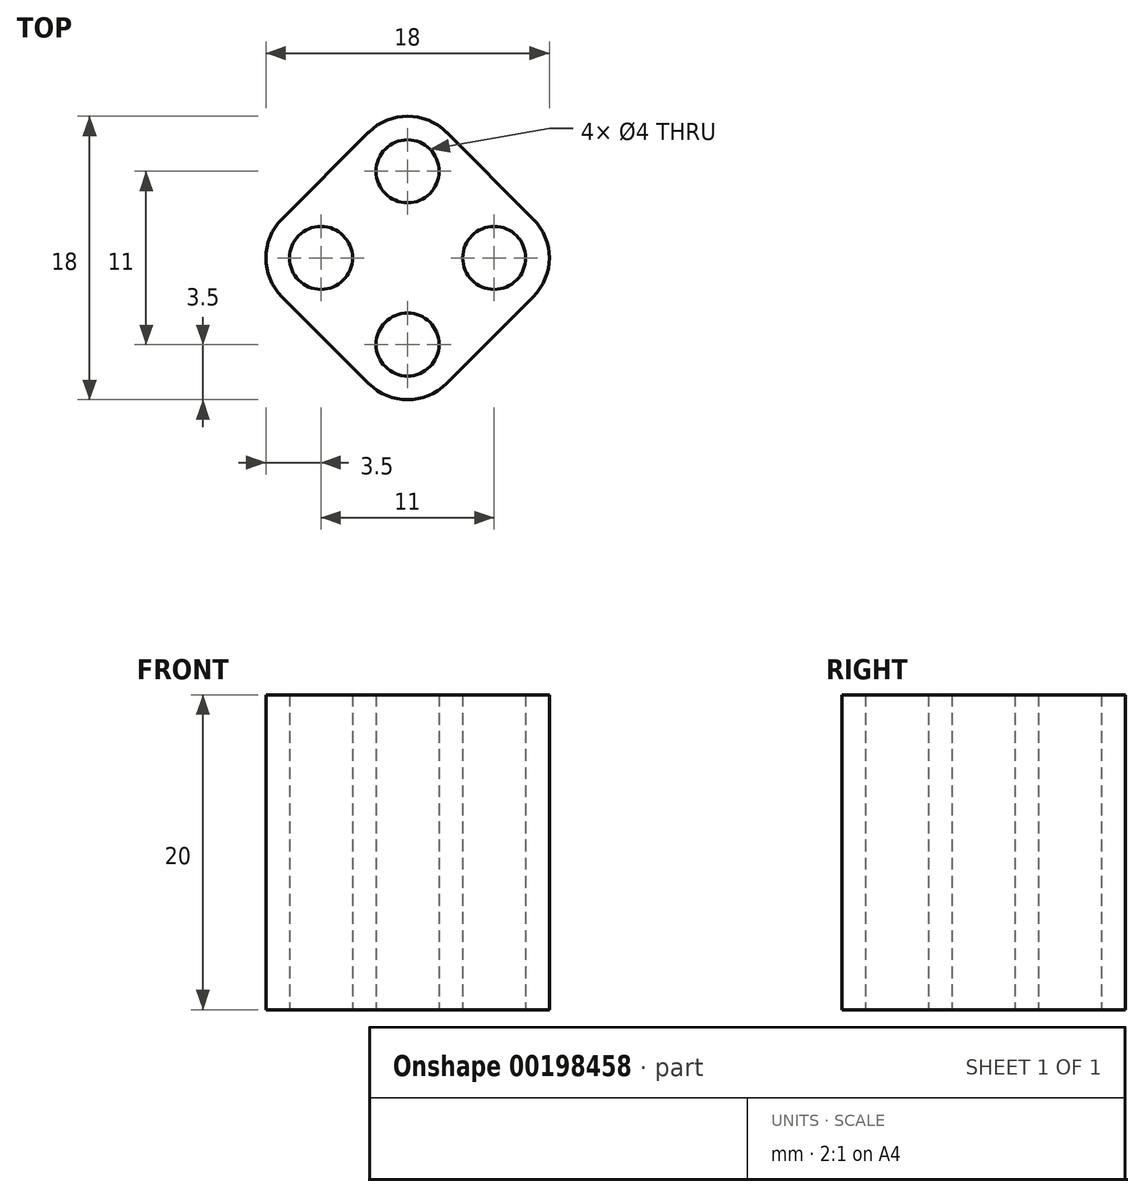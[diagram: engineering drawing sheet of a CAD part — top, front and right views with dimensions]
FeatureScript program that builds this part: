
annotation { "Feature Type Name" : "Feature", "Feature Type Description" : "" }
export const myFeature = defineFeature(function(context is Context, id is Id, definition is map)
    precondition{}
    {
        {
            var Q0;
            Q0=qCreatedBy(makeId("Top.planeOp"),FACE);
            var sketch = newSketch(context, id + "F0", { "sketchPlane" : qUnion([Q0])});
            skArc(sketch, "E0", {"start": v(-7.97, 2.47) * mm, "mid": v(-9, 0) * mm, "end": v(-7.97, -2.47) * mm});
            skCircle(sketch, "E1", {"center": v(-5.5, 0) * mm, "radius": 2 * mm});
            skArc(sketch, "E2.1.0", {"start": v(-2.47, -7.97) * mm, "mid": v(0, -9) * mm, "end": v(2.47, -7.97) * mm});
            skCircle(sketch, "E2.1.1", {"center": v(0, -5.5) * mm, "radius": 2 * mm});
            skArc(sketch, "E2.2.0", {"start": v(7.97, -2.47) * mm, "mid": v(9, 0) * mm, "end": v(7.97, 2.47) * mm});
            skCircle(sketch, "E2.2.1", {"center": v(5.5, 0) * mm, "radius": 2 * mm});
            skArc(sketch, "E2.3.0", {"start": v(2.47, 7.97) * mm, "mid": v(0, 9) * mm, "end": v(-2.47, 7.97) * mm});
            skCircle(sketch, "E2.3.1", {"center": v(0, 5.5) * mm, "radius": 2 * mm});
            skPoint(sketch, "E2.center", {"position": v(0, 0) * mm});
            skLineSegment(sketch, "E3", {"start": v(-7.97, 2.47) * mm, "end": v(-2.47, 7.97) * mm});
            skLineSegment(sketch, "E4", {"start": v(-7.97, -2.47) * mm, "end": v(-2.47, -7.97) * mm});
            skLineSegment(sketch, "E5", {"start": v(2.47, 7.97) * mm, "end": v(7.97, 2.47) * mm});
            skLineSegment(sketch, "E6", {"start": v(7.97, -2.47) * mm, "end": v(2.47, -7.97) * mm});
            skSolve(sketch);
        }
        {
            var Q0;
            Q0=qSketchRegion(id+"F0",true);
            extrude(context, id + "F1", {"entities" : qUnion([Q0]), "depth" : 20 * mm});
        }
    });
